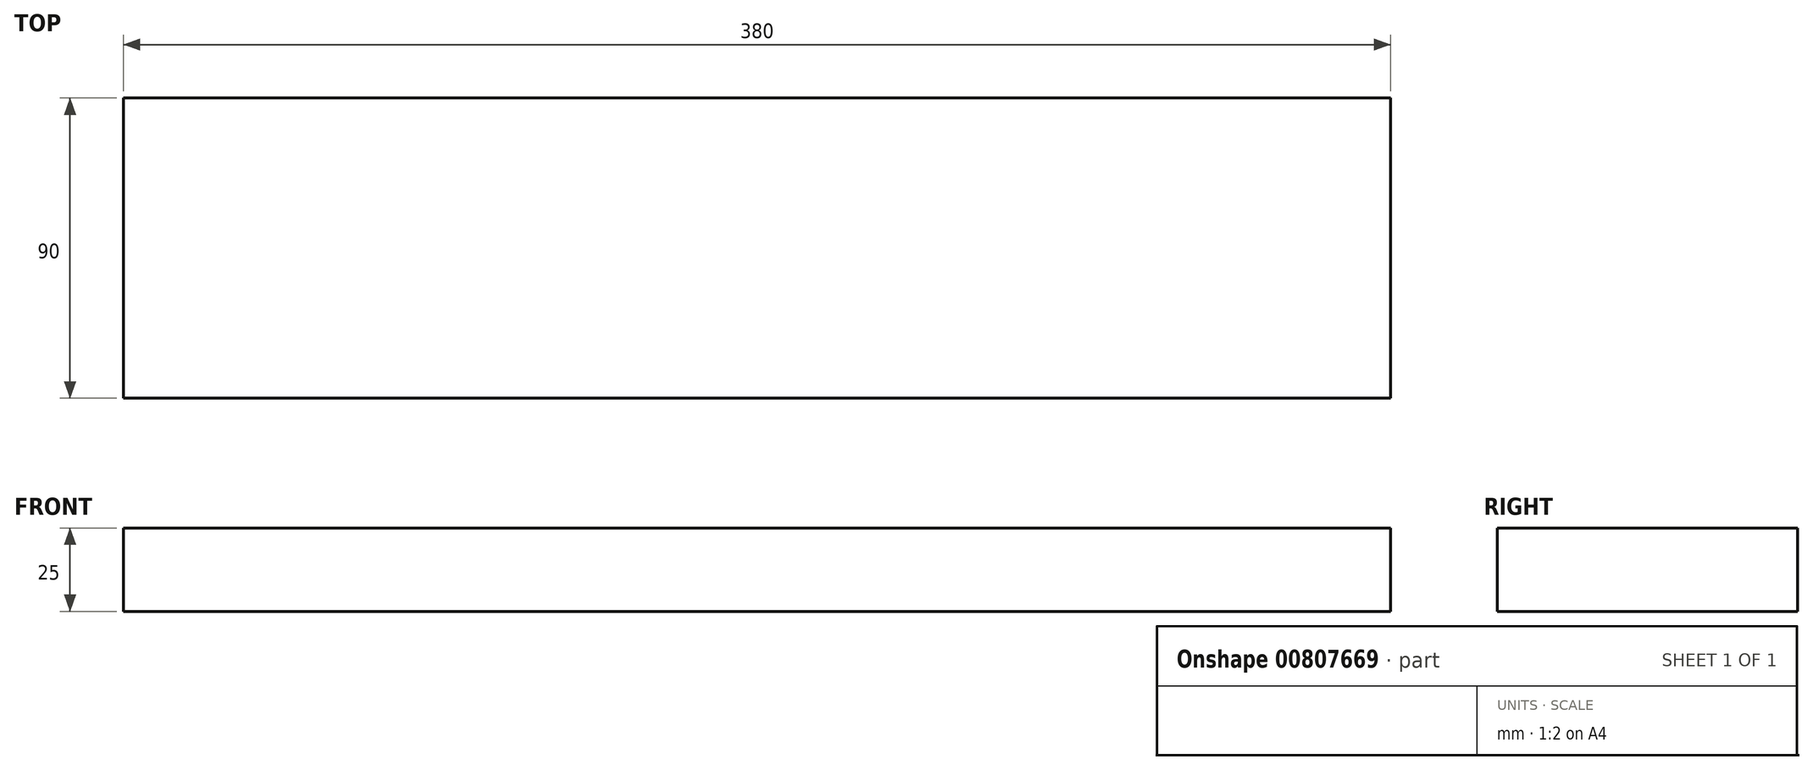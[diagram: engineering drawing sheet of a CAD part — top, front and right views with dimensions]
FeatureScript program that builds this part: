
annotation { "Feature Type Name" : "Feature", "Feature Type Description" : "" }
export const myFeature = defineFeature(function(context is Context, id is Id, definition is map)
    precondition{}
    {
        {
            var Q0;
            Q0=qCreatedBy(makeId("Top.planeOp"),FACE);
            var sketch = newSketch(context, id + "F0", { "sketchPlane" : qUnion([Q0])});
            skLineSegment(sketch, "E0.bottom", {"start": v(190, -45) * mm, "end": v(-190, -45) * mm});
            skLineSegment(sketch, "E0.top", {"start": v(190, 45) * mm, "end": v(-190, 45) * mm});
            skLineSegment(sketch, "E0.left", {"start": v(190, -45) * mm, "end": v(190, 45) * mm});
            skLineSegment(sketch, "E0.right", {"start": v(-190, -45) * mm, "end": v(-190, 45) * mm});
            skPoint(sketch, "E0.middle", {"position": v(0, 0) * mm});
            skSolve(sketch);
        }
        {
            var Q0;
            Q0 = qSketchRegion(id + "F0", true);
            extrude(context, id + "F1", {"entities" : qUnion([Q0]), "depth" : 25 * mm, "offsetDistance" : 25 * mm});
        }
    });
